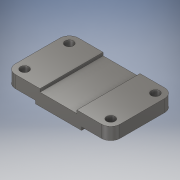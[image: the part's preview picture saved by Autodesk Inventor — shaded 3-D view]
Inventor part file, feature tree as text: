
AUTODESK INVENTOR PART (.ipt)
format: ipt  version: 2019 (Build 230136000, 136)  size: 158,208 bytes
history: native  units: mm
features: extrude x3, sketch x2, fillet x2, mirror x1
ambient origin geometry x8: Origin, YZ Plane, XZ Plane, XY Plane, X Axis, Y Axis, Z Axis, Center Point
bodies: Solid1 (feature_tree)
feature tree (8):
  extrude  "Extrusion1"  Depth=4.0mm
  sketch  "Sketch2"  dims[d2=38.0mm d3=16.0mm d4=44.0mm d5=4.0mm d6=82.0mm d7=0.0mm d8=11.0mm d9=11.0mm d10=12.0mm d11=12.0mm d12=12.0mm d13=12.0mm d14=82.0mm d15=0.0mm d16=82.0mm d17=0.0mm d18=12.0mm d19=12.0mm]
  extrude  "Extrusion2"  Depth=16.0mm
  extrude  "Extrusion3"  Depth=44.0mm
  fillet  "Fillet1"  Radius=4.0mm
  fillet  "Fillet2"  Radius=82.0mm
  mirror  "Mirror1"
  sketch  "Sketch1"  dims[d0=30.0mm d1=4.0mm]
